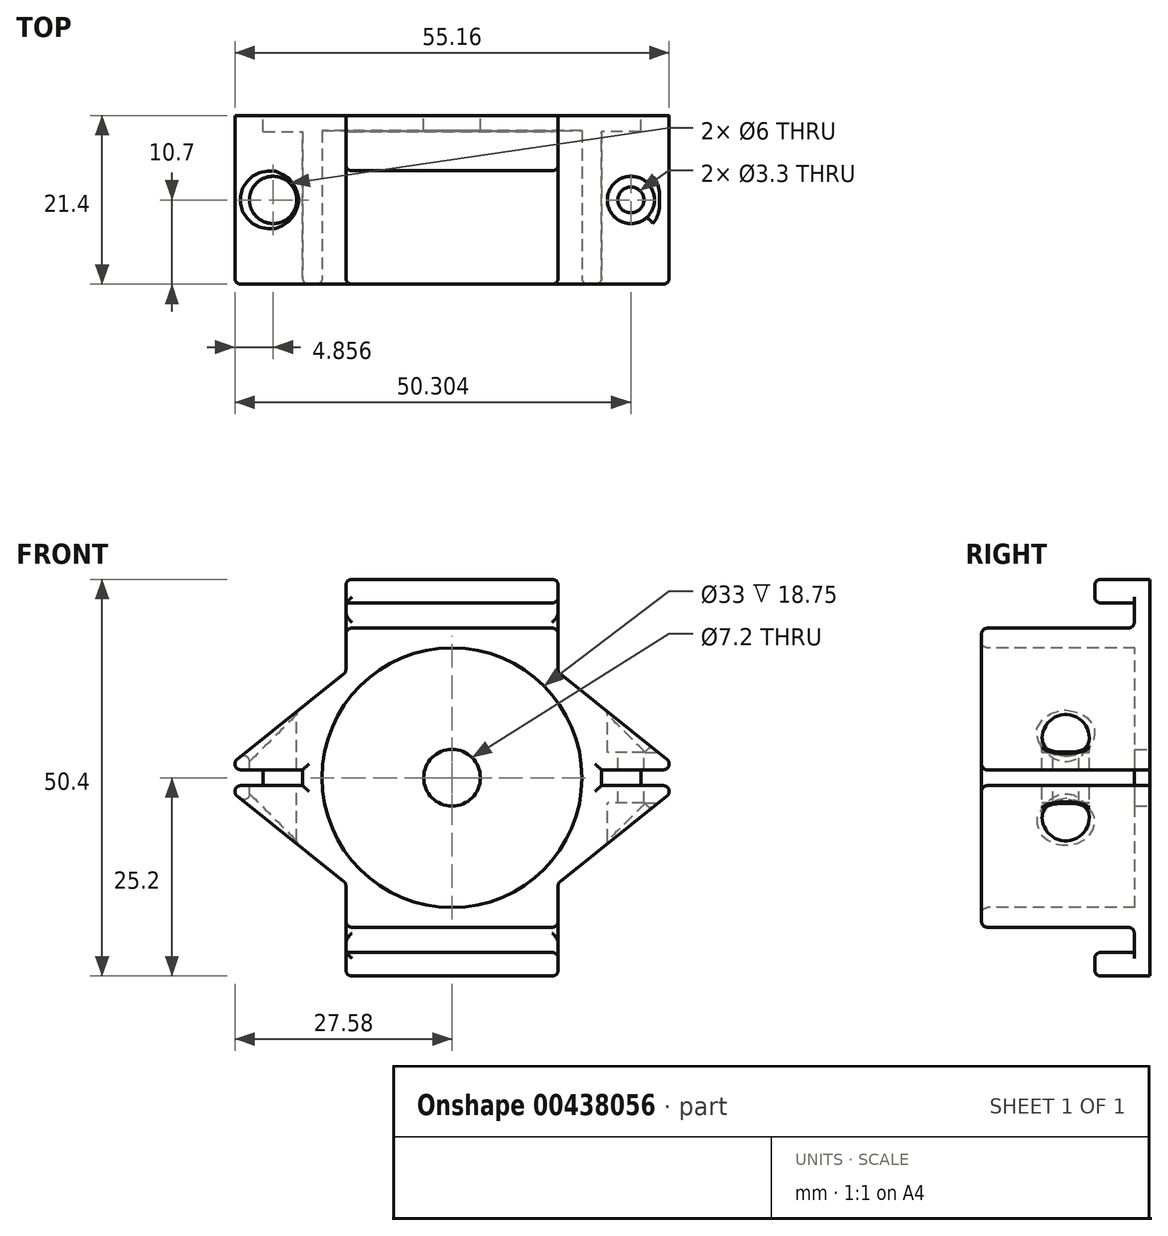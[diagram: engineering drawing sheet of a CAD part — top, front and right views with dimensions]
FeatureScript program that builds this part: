
annotation { "Feature Type Name" : "Feature", "Feature Type Description" : "" }
export const myFeature = defineFeature(function(context is Context, id is Id, definition is map)
    precondition{}
    {
        {
            var Q0;
            Q0=qCreatedBy(makeId("Front.planeOp"),FACE);
            var sketch = newSketch(context, id + "F0", { "sketchPlane" : qUnion([Q0])});
            skCircle(sketch, "E0", {"center": v(0, 0) * mm, "radius": 19 * mm});
            skSolve(sketch);
        }
        {
            var Q0;
            Q0=makeQuery(id+"F0.imprint","IMPRINT",FACE,{"disambiguationData":[TD([[makeQuery(id+"F0.imprint","IMPRINT",EDGE,{"derivedFrom":sQuery(id+"F0.wireOp",EDGE,"E0")}),1.0]])]});
            extrude(context, id + "F1", {"entities" : qUnion([Q0]), "depth" : (19.5 + 1.9) * mm});
        }
        {
            var Q0;
            Q0=makeQuery(id+"F1.opExtrude","CAP_FACE",FACE,{"disambiguationData":[OSD([sQuery(id+"F0.wireOp",EDGE,"E0")])],"isStart":false});
            var sketch = newSketch(context, id + "F2", { "sketchPlane" : qUnion([Q0])});
            skCircle(sketch, "E1", {"center": v(0, 0) * mm, "radius": 16.5 * mm});
            skSolve(sketch);
        }
        {
            var Q0;
            Q0=makeQuery(id+"F2.imprint","IMPRINT",FACE,{"disambiguationData":[TD([[makeQuery(id+"F2.imprint","IMPRINT",EDGE,{"derivedFrom":sQuery(id+"F2.wireOp",EDGE,"E1")}),1.0]])]});
            var Q1;
            Q1=sQuery(id+"F2.wireOp",EDGE,"E1");
            extrude(context, id + "F3", {"entities" : qUnion([Q0]), "operationType" : NewBodyOperationType.REMOVE, "surfaceEntities" : qUnion([Q1]), "oppositeDirection" : true, "depth" : 19.5 * mm});
        }
        {
            var Q0;
            Q0=makeQuery(id+"F0.imprint","IMPRINT",FACE,{"disambiguationData":[TD([[makeQuery(id+"F0.imprint","IMPRINT",EDGE,{"derivedFrom":sQuery(id+"F0.wireOp",EDGE,"E0")}),1.0]])]});
            var sketch = newSketch(context, id + "F4", { "sketchPlane" : qUnion([Q0])});
            skCircle(sketch, "E2", {"center": v(0, 0) * mm, "radius": 3.6 * mm});
            skSolve(sketch);
        }
        {
            var Q0;
            Q0=makeQuery(id+"F4.imprint","IMPRINT",FACE,{"disambiguationData":[TD([[makeQuery(id+"F4.imprint","IMPRINT",EDGE,{"derivedFrom":sQuery(id+"F4.wireOp",EDGE,"E2")}),1.0]])]});
            extrude(context, id + "F5", {"entities" : qUnion([Q0]), "operationType" : NewBodyOperationType.REMOVE, "oppositeDirection" : true, "depth" : -1.9 * mm});
        }
        {
            var Q0;
            {var subQ0=sQuery(id+"F0.wireOp",EDGE,"E0");Q0=makeQuery(id+"F8.boolean.opBoolean","MERGE",FACE,{"derivedFrom":[makeQuery(id+"F1.opExtrude","CAP_FACE",FACE,{"disambiguationData":[OSD([subQ0])],"isStart":false}),makeQuery(id+"F8.opExtrude","CAP_FACE",FACE,{"disambiguationData":[OSD([subQ0,sQuery(id+"F7.wireOp",EDGE,"JnGJQQhQ-O3qH-GfFH-OKy3-jtoUdUrH5ozl"),sQuery(id+"F7.wireOp",EDGE,"E11")])],"isStart":true}),makeQuery(id+"F8.opExtrude","CAP_FACE",FACE,{"disambiguationData":[OSD([subQ0,sQuery(id+"F7.wireOp",EDGE,"b05943de-8eb0-47d5-9eb4-3e9c2a586c67.1.1"),sQuery(id+"F7.wireOp",EDGE,"b05943de-8eb0-47d5-9eb4-3e9c2a586c67.1.2")])],"isStart":true}),makeQuery(id+"F8.opExtrude","CAP_FACE",FACE,{"disambiguationData":[OSD([subQ0,sQuery(id+"F7.wireOp",EDGE,"76fbe852-51aa-46ac-98ce-1b56ffee6fad0.MirrorCS"),sQuery(id+"F7.wireOp",EDGE,"c90fd7eb-af4d-439f-be0f-882f93c487a10.MirrorCS")])],"isStart":true}),makeQuery(id+"F8.opExtrude","CAP_FACE",FACE,{"disambiguationData":[OSD([subQ0,sQuery(id+"F7.wireOp",EDGE,"384a4ab6-6deb-44a3-bccf-448af2679dce0.MirrorCS"),sQuery(id+"F7.wireOp",EDGE,"9e9dcbe8-0e53-4627-bc9e-6be6067dd5380.MirrorCS")])],"isStart":true})]});}
            var sketch = newSketch(context, id + "F6", { "sketchPlane" : qUnion([Q0])});
            skPoint(sketch, "E3.oppositeSnap0", {"position": v(0, 19) * mm});
            skLineSegment(sketch, "E3.top", {"start": v(-13.48, 19) * mm, "end": v(13.48, 19) * mm});
            skLineSegment(sketch, "E3.left", {"start": v(-13.48, 13.39) * mm, "end": v(-13.48, 19) * mm});
            skLineSegment(sketch, "E3.right", {"start": v(13.48, 13.39) * mm, "end": v(13.48, 19) * mm});
            skLineSegment(sketch, "E4", {"start": v(0, 19) * mm, "end": v(13.48, 13.39) * mm});
            skLineSegment(sketch, "E5", {"start": v(0, 19) * mm, "end": v(-13.48, 13.39) * mm});
            skLineSegment(sketch, "E6.MirrorCS", {"start": v(-13.48, -19) * mm, "end": v(13.48, -19) * mm});
            skLineSegment(sketch, "E7.MirrorCS", {"start": v(13.48, -13.39) * mm, "end": v(13.48, -19) * mm});
            skLineSegment(sketch, "E8.MirrorCS", {"start": v(0, -19) * mm, "end": v(13.48, -13.39) * mm});
            skLineSegment(sketch, "E9.MirrorCS", {"start": v(0, -19) * mm, "end": v(-13.48, -13.39) * mm});
            skLineSegment(sketch, "E10.MirrorCS", {"start": v(-13.48, -13.39) * mm, "end": v(-13.48, -19) * mm});
            skSolve(sketch);
        }
        {
            var Q0;
            Q0=makeQuery(id+"F1.opExtrude","CAP_FACE",FACE,{"disambiguationData":[OSD([sQuery(id+"F0.wireOp",EDGE,"E0")])],"isStart":false});
            var sketch = newSketch(context, id + "F7", { "sketchPlane" : qUnion([Q0])});
            skLineSegment(sketch, "E11", {"start": v(28.97, 1) * mm, "end": v(18.97, 1) * mm});
            skLineSegment(sketch, "E12", {"start": v(18.97, 1) * mm, "end": v(13.48, 13.39) * mm});
            skLineSegment(sketch, "E13", {"start": v(13.48, 13.39) * mm, "end": v(28.97, 1) * mm});
            skLineSegment(sketch, "E14.MirrorCS", {"start": v(-18.97, 1) * mm, "end": v(-13.48, 13.39) * mm});
            skLineSegment(sketch, "E15.MirrorCS", {"start": v(-13.48, 13.39) * mm, "end": v(-28.97, 1) * mm});
            skLineSegment(sketch, "E16.MirrorCS", {"start": v(-28.97, 1) * mm, "end": v(-18.97, 1) * mm});
            skLineSegment(sketch, "E17.MirrorCS", {"start": v(28.97, -1) * mm, "end": v(18.97, -1) * mm});
            skLineSegment(sketch, "E18.MirrorCS", {"start": v(13.48, -13.39) * mm, "end": v(28.97, -1) * mm});
            skLineSegment(sketch, "E19.MirrorCS", {"start": v(18.97, -1) * mm, "end": v(13.48, -13.39) * mm});
            skLineSegment(sketch, "E20.MirrorCS", {"start": v(-18.97, -1) * mm, "end": v(-13.48, -13.39) * mm});
            skLineSegment(sketch, "E21.MirrorCS", {"start": v(-13.48, -13.39) * mm, "end": v(-28.97, -1) * mm});
            skLineSegment(sketch, "E22.MirrorCS", {"start": v(-28.97, -1) * mm, "end": v(-18.97, -1) * mm});
            skSolve(sketch);
        }
        {
            var Q0;
            {var subQ0=sQuery(id+"F7.wireOp",EDGE,"JnGJQQhQ-O3qH-GfFH-OKy3-jtoUdUrH5ozl");Q0=makeQuery(id+"F7.imprint","IMPRINT",FACE,{"disambiguationData":[TD([[makeQuery(id+"F7.imprint","IMPRINT",EDGE,{"derivedFrom":subQ0}),-1.0]])]});}
            var Q1;
            {var subQ0=sQuery(id+"F7.wireOp",EDGE,"b05943de-8eb0-47d5-9eb4-3e9c2a586c67.1.1");Q1=makeQuery(id+"F7.imprint","IMPRINT",FACE,{"disambiguationData":[TD([[makeQuery(id+"F7.imprint","IMPRINT",EDGE,{"derivedFrom":subQ0}),-1.0]])]});}
            var Q2;
            {var subQ0=sQuery(id+"F7.wireOp",EDGE,"76fbe852-51aa-46ac-98ce-1b56ffee6fad0.MirrorCS");Q2=makeQuery(id+"F7.imprint","IMPRINT",FACE,{"disambiguationData":[TD([[makeQuery(id+"F7.imprint","IMPRINT",EDGE,{"derivedFrom":subQ0}),1.0]])]});}
            var Q3;
            {var subQ0=sQuery(id+"F7.wireOp",EDGE,"384a4ab6-6deb-44a3-bccf-448af2679dce0.MirrorCS");Q3=makeQuery(id+"F7.imprint","IMPRINT",FACE,{"disambiguationData":[TD([[makeQuery(id+"F7.imprint","IMPRINT",EDGE,{"derivedFrom":subQ0}),1.0]])]});}
            var Q4;
            {var subQ0=sQuery(id+"F6.wireOp",EDGE,"E3.left");Q4=makeQuery(id+"F6.imprint","IMPRINT",FACE,{"disambiguationData":[TD([[makeQuery(id+"F6.imprint","IMPRINT",EDGE,{"derivedFrom":subQ0}),-1.0]])]});}
            var Q5;
            {var subQ0=sQuery(id+"F6.wireOp",EDGE,"E3.right");Q5=makeQuery(id+"F6.imprint","IMPRINT",FACE,{"disambiguationData":[TD([[makeQuery(id+"F6.imprint","IMPRINT",EDGE,{"derivedFrom":subQ0}),1.0]])]});}
            var Q6;
            {var subQ0=sQuery(id+"F6.wireOp",EDGE,"E10.MirrorCS");Q6=makeQuery(id+"F6.imprint","IMPRINT",FACE,{"disambiguationData":[TD([[makeQuery(id+"F6.imprint","IMPRINT",EDGE,{"derivedFrom":subQ0}),1.0]])]});}
            var Q7;
            {var subQ0=sQuery(id+"F6.wireOp",EDGE,"E7.MirrorCS");Q7=makeQuery(id+"F6.imprint","IMPRINT",FACE,{"disambiguationData":[TD([[makeQuery(id+"F6.imprint","IMPRINT",EDGE,{"derivedFrom":subQ0}),-1.0]])]});}
            var Q8;
            {var subQ0=sQuery(id+"F7.wireOp",EDGE,"E15.MirrorCS");Q8=makeQuery(id+"F7.imprint","IMPRINT",FACE,{"disambiguationData":[TD([[makeQuery(id+"F7.imprint","IMPRINT",EDGE,{"derivedFrom":subQ0}),1.0]])]});}
            var Q9;
            {var subQ0=sQuery(id+"F7.wireOp",EDGE,"E21.MirrorCS");Q9=makeQuery(id+"F7.imprint","IMPRINT",FACE,{"disambiguationData":[TD([[makeQuery(id+"F7.imprint","IMPRINT",EDGE,{"derivedFrom":subQ0}),-1.0]])]});}
            var Q10;
            {var subQ0=sQuery(id+"F7.wireOp",EDGE,"E17.MirrorCS");Q10=makeQuery(id+"F7.imprint","IMPRINT",FACE,{"disambiguationData":[TD([[makeQuery(id+"F7.imprint","IMPRINT",EDGE,{"derivedFrom":subQ0}),1.0]])]});}
            var Q11;
            {var subQ0=sQuery(id+"F7.wireOp",EDGE,"E11");Q11=makeQuery(id+"F7.imprint","IMPRINT",FACE,{"disambiguationData":[TD([[makeQuery(id+"F7.imprint","IMPRINT",EDGE,{"derivedFrom":subQ0}),-1.0]])]});}
            var Q12;
            Q12=makeQuery(id+"F1.opExtrude","SWEPT_FACE",FACE,{"disambiguationData":[OSD([sQuery(id+"F0.wireOp",EDGE,"E0")])]});
            extrude(context, id + "F8", {"entities" : qUnion([Q0, Q1, Q2, Q3, Q4, Q5, Q6, Q7, Q8, Q9, Q10, Q11]), "operationType" : NewBodyOperationType.ADD, "oppositeDirection" : true, "endBoundEntityFace" : qUnion([Q12]), "depth" : (19.5 + 1.9) * mm});
        }
        {
            var Q0;
            Q0=qCreatedBy(makeId("Top.planeOp"),FACE);
            var sketch = newSketch(context, id + "F9", { "sketchPlane" : qUnion([Q0])});
            skCircle(sketch, "E23", {"center": v(22.72, -10.7) * mm, "radius": 3 * mm});
            skCircle(sketch, "E24.MirrorC", {"center": v(-22.72, -10.7) * mm, "radius": 3 * mm});
            skSolve(sketch);
        }
        {
            var Q0;
            Q0 = qSketchRegion(id + "F9", true);
            extrude(context, id + "F10", {"entities" : qUnion([Q0]), "operationType" : NewBodyOperationType.REMOVE, "oppositeDirection" : true, "depth" : 20.52 * mm, "symmetric" : true});
        }
        {
            var Q0;
            Q0=makeQuery(id+"F9.imprint","IMPRINT",FACE,{"disambiguationData":[TD([[makeQuery(id+"F9.imprint","IMPRINT",EDGE,{"derivedFrom":sQuery(id+"F9.wireOp",EDGE,"E23")}),1.0]])]});
            var Q1;
            Q1=makeQuery(id+"F9.imprint","IMPRINT",FACE,{"disambiguationData":[TD([[makeQuery(id+"F9.imprint","IMPRINT",EDGE,{"derivedFrom":sQuery(id+"F9.wireOp",EDGE,"E24.MirrorC")}),-1.0]])]});
            extrude(context, id + "F11", {"entities" : qUnion([Q0, Q1]), "operationType" : NewBodyOperationType.ADD, "oppositeDirection" : true, "depth" : 6.44 * mm, "symmetric" : true});
        }
        {
            var Q0;
            Q0 = qSketchRegion(id + "F9", true);
            extrude(context, id + "F12", {"entities" : qUnion([Q0]), "operationType" : NewBodyOperationType.REMOVE, "depth" : 2 * mm, "symmetric" : true});
        }
        {
            var Q0;
            Q0=qCreatedBy(makeId("Top.planeOp"),FACE);
            var sketch = newSketch(context, id + "F13", { "sketchPlane" : qUnion([Q0])});
            skCircle(sketch, "E25", {"center": v(22.72, -10.7) * mm, "radius": 1.65 * mm});
            skCircle(sketch, "E26.MirrorC", {"center": v(-22.72, -10.7) * mm, "radius": 1.65 * mm});
            skSolve(sketch);
        }
        {
            var Q0;
            Q0=makeQuery(id+"F13.imprint","IMPRINT",FACE,{"disambiguationData":[TD([[makeQuery(id+"F13.imprint","IMPRINT",EDGE,{"derivedFrom":sQuery(id+"F13.wireOp",EDGE,"E25")}),1.0]])]});
            var Q1;
            Q1=makeQuery(id+"F13.imprint","IMPRINT",FACE,{"disambiguationData":[TD([[makeQuery(id+"F13.imprint","IMPRINT",EDGE,{"derivedFrom":sQuery(id+"F13.wireOp",EDGE,"E26.MirrorC")}),-1.0]])]});
            extrude(context, id + "F14", {"entities" : qUnion([Q0, Q1]), "operationType" : NewBodyOperationType.REMOVE, "oppositeDirection" : true, "depth" : 20 * mm, "symmetric" : true});
        }
        {
            var Q0;
            {var subQ0=sQuery(id+"F6.wireOp",EDGE,"E6.MirrorCS");var subQ1=sQuery(id+"F0.wireOp",EDGE,"E0");var subQ2=sQuery(id+"F6.wireOp",EDGE,"E3.top");Q0=makeQuery(id+"F8.boolean.opBoolean","MERGE",FACE,{"derivedFrom":[makeQuery(id+"F1.opExtrude","CAP_FACE",FACE,{"disambiguationData":[OSD([subQ1])],"isStart":true}),makeQuery(id+"F8.opExtrude","CAP_FACE",FACE,{"disambiguationData":[OSD([subQ1,sQuery(id+"F7.wireOp",EDGE,"JnGJQQhQ-O3qH-GfFH-OKy3-jtoUdUrH5ozl"),sQuery(id+"F7.wireOp",EDGE,"E11")])],"isStart":false}),makeQuery(id+"F8.opExtrude","CAP_FACE",FACE,{"disambiguationData":[OSD([subQ1,sQuery(id+"F7.wireOp",EDGE,"b05943de-8eb0-47d5-9eb4-3e9c2a586c67.1.1"),sQuery(id+"F7.wireOp",EDGE,"b05943de-8eb0-47d5-9eb4-3e9c2a586c67.1.2")])],"isStart":false}),makeQuery(id+"F8.opExtrude","CAP_FACE",FACE,{"disambiguationData":[OSD([subQ1,sQuery(id+"F7.wireOp",EDGE,"76fbe852-51aa-46ac-98ce-1b56ffee6fad0.MirrorCS"),sQuery(id+"F7.wireOp",EDGE,"c90fd7eb-af4d-439f-be0f-882f93c487a10.MirrorCS")])],"isStart":false}),makeQuery(id+"F8.opExtrude","CAP_FACE",FACE,{"disambiguationData":[OSD([subQ1,sQuery(id+"F7.wireOp",EDGE,"384a4ab6-6deb-44a3-bccf-448af2679dce0.MirrorCS"),sQuery(id+"F7.wireOp",EDGE,"9e9dcbe8-0e53-4627-bc9e-6be6067dd5380.MirrorCS")])],"isStart":false}),makeQuery(id+"F8.opExtrude","CAP_FACE",FACE,{"disambiguationData":[OSD([subQ1,subQ2,sQuery(id+"F6.wireOp",EDGE,"E3.left")])],"isStart":false}),makeQuery(id+"F8.opExtrude","CAP_FACE",FACE,{"disambiguationData":[OSD([subQ1,subQ2,sQuery(id+"F6.wireOp",EDGE,"E3.right")])],"isStart":false}),makeQuery(id+"F8.opExtrude","CAP_FACE",FACE,{"disambiguationData":[OSD([subQ1,subQ0,sQuery(id+"F6.wireOp",EDGE,"E10.MirrorCS")])],"isStart":false}),makeQuery(id+"F8.opExtrude","CAP_FACE",FACE,{"disambiguationData":[OSD([subQ1,subQ0,sQuery(id+"F6.wireOp",EDGE,"E7.MirrorCS")])],"isStart":false})]});}
            var sketch = newSketch(context, id + "F15", { "sketchPlane" : qUnion([Q0])});
            skLineSegment(sketch, "E27.bottom", {"start": v(-13.48, 19) * mm, "end": v(13.48, 19) * mm});
            skLineSegment(sketch, "E27.top", {"start": v(-13.48, 22.2) * mm, "end": v(13.48, 22.2) * mm});
            skLineSegment(sketch, "E27.left", {"start": v(-13.48, 19) * mm, "end": v(-13.48, 22.2) * mm});
            skLineSegment(sketch, "E27.right", {"start": v(13.48, 19) * mm, "end": v(13.48, 22.2) * mm});
            skLineSegment(sketch, "E28.MirrorCS", {"start": v(-13.48, -19) * mm, "end": v(-13.48, -22.2) * mm});
            skLineSegment(sketch, "E29.MirrorCS", {"start": v(-13.48, -22.2) * mm, "end": v(13.48, -22.2) * mm});
            skLineSegment(sketch, "E30.MirrorCS", {"start": v(-13.48, -19) * mm, "end": v(13.48, -19) * mm});
            skLineSegment(sketch, "E31.MirrorCS", {"start": v(13.48, -19) * mm, "end": v(13.48, -22.2) * mm});
            skLineSegment(sketch, "E32.bottom", {"start": v(-18.97, 1) * mm, "end": v(-23.97, 1) * mm});
            skLineSegment(sketch, "E32.top", {"start": v(-18.97, -1) * mm, "end": v(-23.97, -1) * mm});
            skLineSegment(sketch, "E32.left", {"start": v(-18.97, 1) * mm, "end": v(-18.97, -1) * mm});
            skLineSegment(sketch, "E32.right", {"start": v(-23.97, 1) * mm, "end": v(-23.97, -1) * mm});
            skPoint(sketch, "E33", {"position": v(-23.97, 1) * mm});
            skPoint(sketch, "E34", {"position": v(-23.97, -1) * mm});
            skLineSegment(sketch, "E35.bottom", {"start": v(18.97, 1) * mm, "end": v(23.97, 1) * mm});
            skLineSegment(sketch, "E35.top", {"start": v(18.97, -1) * mm, "end": v(23.97, -1) * mm});
            skLineSegment(sketch, "E35.left", {"start": v(18.97, 1) * mm, "end": v(18.97, -1) * mm});
            skLineSegment(sketch, "E35.right", {"start": v(23.97, 1) * mm, "end": v(23.97, -1) * mm});
            skPoint(sketch, "E36", {"position": v(23.97, 1) * mm});
            skPoint(sketch, "E37", {"position": v(23.97, -1) * mm});
            skSolve(sketch);
        }
        {
            var Q0;
            Q0=makeQuery(id+"F15.imprint","IMPRINT",FACE,{"disambiguationData":[TD([[makeQuery(id+"F15.imprint","IMPRINT",EDGE,{"derivedFrom":sQuery(id+"F15.wireOp",EDGE,"E27.bottom")}),-1.0]])]});
            var sketch = newSketch(context, id + "F16", { "sketchPlane" : qUnion([Q0])});
            skLineSegment(sketch, "E38.bottom", {"start": v(-13.48, 22.2) * mm, "end": v(13.48, 22.2) * mm});
            skLineSegment(sketch, "E38.top", {"start": v(-13.48, 25.2) * mm, "end": v(13.48, 25.2) * mm});
            skLineSegment(sketch, "E38.left", {"start": v(-13.48, 22.2) * mm, "end": v(-13.48, 25.2) * mm});
            skLineSegment(sketch, "E38.right", {"start": v(13.48, 22.2) * mm, "end": v(13.48, 25.2) * mm});
            skLineSegment(sketch, "E39.MirrorCS", {"start": v(-13.48, -22.2) * mm, "end": v(13.48, -22.2) * mm});
            skLineSegment(sketch, "E40.MirrorCS", {"start": v(13.48, -22.2) * mm, "end": v(13.48, -25.2) * mm});
            skLineSegment(sketch, "E41.MirrorCS", {"start": v(-13.48, -25.2) * mm, "end": v(13.48, -25.2) * mm});
            skLineSegment(sketch, "E42.MirrorCS", {"start": v(-13.48, -22.2) * mm, "end": v(-13.48, -25.2) * mm});
            skSolve(sketch);
        }
        {
            var Q0;
            Q0=makeQuery(id+"F15.imprint","IMPRINT",FACE,{"disambiguationData":[TD([[makeQuery(id+"F15.imprint","IMPRINT",EDGE,{"derivedFrom":sQuery(id+"F15.wireOp",EDGE,"E27.bottom")}),-1.0]])]});
            var Q1;
            Q1=makeQuery(id+"F15.imprint","IMPRINT",FACE,{"disambiguationData":[TD([[makeQuery(id+"F15.imprint","IMPRINT",EDGE,{"derivedFrom":sQuery(id+"F15.wireOp",EDGE,"pVymzZib-BWJs-xoJs-sTC6-ayV31QzRr0Km.bottom")}),1.0]])]});
            var Q2;
            Q2=makeQuery(id+"F15.imprint","IMPRINT",FACE,{"disambiguationData":[TD([[makeQuery(id+"F15.imprint","IMPRINT",EDGE,{"derivedFrom":sQuery(id+"F15.wireOp",EDGE,"E28.MirrorCS")}),1.0]])]});
            var Q3;
            Q3=makeQuery(id+"F15.imprint","IMPRINT",FACE,{"disambiguationData":[TD([[makeQuery(id+"F15.imprint","IMPRINT",EDGE,{"derivedFrom":sQuery(id+"F15.wireOp",EDGE,"p6bBq81N-0zO1-3e9F-RNQn-4i8wIQgML4Y9.bottom")}),-1.0]])]});
            var Q4;
            Q4=makeQuery(id+"F15.imprint","IMPRINT",FACE,{"disambiguationData":[TD([[makeQuery(id+"F15.imprint","IMPRINT",EDGE,{"derivedFrom":sQuery(id+"F15.wireOp",EDGE,"SPB9DOaG-sIQF-bfla-kVRV-wDr5gLPkeSE0.bottom")}),1.0]])]});
            var Q5;
            Q5=makeQuery(id+"F15.imprint","IMPRINT",FACE,{"disambiguationData":[TD([[makeQuery(id+"F15.imprint","IMPRINT",EDGE,{"derivedFrom":sQuery(id+"F15.wireOp",EDGE,"49c1c15a-7392-4b62-8206-24bcfd820ca90.MirrorCS")}),1.0]])]});
            var Q6;
            Q6=makeQuery(id+"F15.imprint","IMPRINT",FACE,{"disambiguationData":[TD([[makeQuery(id+"F15.imprint","IMPRINT",EDGE,{"derivedFrom":sQuery(id+"F15.wireOp",EDGE,"E35.bottom")}),1.0]])]});
            var Q7;
            Q7=makeQuery(id+"F15.imprint","IMPRINT",FACE,{"disambiguationData":[TD([[makeQuery(id+"F15.imprint","IMPRINT",EDGE,{"derivedFrom":sQuery(id+"F15.wireOp",EDGE,"E32.bottom")}),-1.0]])]});
            extrude(context, id + "F17", {"entities" : qUnion([Q0, Q1, Q2, Q3, Q4, Q5, Q6, Q7]), "operationType" : NewBodyOperationType.ADD, "oppositeDirection" : true, "depth" : 2 * mm});
        }
        {
            var Q0;
            Q0=makeQuery(id+"F16.imprint","IMPRINT",FACE,{"disambiguationData":[TD([[makeQuery(id+"F16.imprint","IMPRINT",EDGE,{"derivedFrom":sQuery(id+"F16.wireOp",EDGE,"E39.MirrorCS")}),-1.0]])]});
            var Q1;
            Q1=makeQuery(id+"F16.imprint","IMPRINT",FACE,{"disambiguationData":[TD([[makeQuery(id+"F16.imprint","IMPRINT",EDGE,{"derivedFrom":sQuery(id+"F16.wireOp",EDGE,"E38.bottom")}),1.0]])]});
            extrude(context, id + "F18", {"entities" : qUnion([Q0, Q1]), "operationType" : NewBodyOperationType.ADD, "oppositeDirection" : true, "depth" : 7 * mm});
        }
        {
            var Q0;
            {var subQ0=sQuery(id+"F0.wireOp",EDGE,"E0");var subQ1=sQuery(id+"F6.wireOp",EDGE,"E6.MirrorCS");var subQ2=sQuery(id+"F6.wireOp",EDGE,"E3.top");Q0=makeQuery(id+"F8.boolean.opBoolean","MERGE",FACE,{"derivedFrom":[makeQuery(id+"F1.opExtrude","CAP_FACE",FACE,{"disambiguationData":[OSD([subQ0])],"isStart":false}),makeQuery(id+"F8.opExtrude","CAP_FACE",FACE,{"disambiguationData":[OSD([subQ0,subQ2,sQuery(id+"F6.wireOp",EDGE,"E3.left")])],"isStart":true}),makeQuery(id+"F8.opExtrude","CAP_FACE",FACE,{"disambiguationData":[OSD([subQ0,subQ2,sQuery(id+"F6.wireOp",EDGE,"E3.right")])],"isStart":true}),makeQuery(id+"F8.opExtrude","CAP_FACE",FACE,{"disambiguationData":[OSD([subQ0,subQ1,sQuery(id+"F6.wireOp",EDGE,"E10.MirrorCS")])],"isStart":true}),makeQuery(id+"F8.opExtrude","CAP_FACE",FACE,{"disambiguationData":[OSD([subQ0,subQ1,sQuery(id+"F6.wireOp",EDGE,"E7.MirrorCS")])],"isStart":true}),makeQuery(id+"F8.opExtrude","CAP_FACE",FACE,{"disambiguationData":[OSD([subQ0,sQuery(id+"F7.wireOp",EDGE,"E11"),sQuery(id+"F7.wireOp",EDGE,"E13")])],"isStart":true}),makeQuery(id+"F8.opExtrude","CAP_FACE",FACE,{"disambiguationData":[OSD([subQ0,sQuery(id+"F7.wireOp",EDGE,"E15.MirrorCS"),sQuery(id+"F7.wireOp",EDGE,"E16.MirrorCS")])],"isStart":true}),makeQuery(id+"F8.opExtrude","CAP_FACE",FACE,{"disambiguationData":[OSD([subQ0,sQuery(id+"F7.wireOp",EDGE,"E17.MirrorCS"),sQuery(id+"F7.wireOp",EDGE,"E18.MirrorCS")])],"isStart":true}),makeQuery(id+"F8.opExtrude","CAP_FACE",FACE,{"disambiguationData":[OSD([subQ0,sQuery(id+"F7.wireOp",EDGE,"E21.MirrorCS"),sQuery(id+"F7.wireOp",EDGE,"E22.MirrorCS")])],"isStart":true})]});}
            var Q1;
            Q1=makeQuery(id+"F10.boolean.opBoolean","INTERSECT",EDGE,{"derivedFrom":[makeQuery(id+"F8.opExtrude","SWEPT_FACE",FACE,{"disambiguationData":[OSD([sQuery(id+"F7.wireOp",EDGE,"E18.MirrorCS")])]}),makeQuery(id+"F10.opExtrude","SWEPT_FACE",FACE,{"disambiguationData":[OSD([sQuery(id+"F9.wireOp",EDGE,"E23")])]})]});
            var Q2;
            Q2=makeQuery(id+"F10.boolean.opBoolean","INTERSECT",EDGE,{"derivedFrom":[makeQuery(id+"F8.opExtrude","SWEPT_FACE",FACE,{"disambiguationData":[OSD([sQuery(id+"F7.wireOp",EDGE,"E13")])]}),makeQuery(id+"F10.opExtrude","SWEPT_FACE",FACE,{"disambiguationData":[OSD([sQuery(id+"F9.wireOp",EDGE,"E23")])]})]});
            var Q3;
            Q3=makeQuery(id+"F18.opExtrude","CAP_FACE",FACE,{"disambiguationData":[OSD([sQuery(id+"F16.wireOp",EDGE,"E39.MirrorCS"),sQuery(id+"F16.wireOp",EDGE,"E40.MirrorCS"),sQuery(id+"F16.wireOp",EDGE,"E41.MirrorCS"),sQuery(id+"F16.wireOp",EDGE,"E42.MirrorCS")])],"isStart":false});
            var Q4;
            {var subQ0=sQuery(id+"F6.wireOp",EDGE,"E6.MirrorCS");Q4=makeQuery(id+"F8.boolean.opBoolean","MERGE",FACE,{"derivedFrom":[makeQuery(id+"F8.opExtrude","SWEPT_FACE",FACE,{"disambiguationData":[OSD([subQ0]),TDD([makeQuery(id+"F6.imprint","IMPRINT",EDGE,{"disambiguationData":[TD([[makeQuery(id+"F6.imprint","INTERSECT",VERTEX,{"derivedFrom":[subQ0,sQuery(id+"F6.wireOp",EDGE,"E10.MirrorCS")]}),-1.0]])],"derivedFrom":subQ0})])]}),makeQuery(id+"F8.opExtrude","SWEPT_FACE",FACE,{"disambiguationData":[OSD([subQ0]),TDD([makeQuery(id+"F6.imprint","IMPRINT",EDGE,{"disambiguationData":[TD([[makeQuery(id+"F6.imprint","INTERSECT",VERTEX,{"derivedFrom":[subQ0,sQuery(id+"F6.wireOp",EDGE,"E7.MirrorCS")]}),1.0]])],"derivedFrom":subQ0})])]})]});}
            var Q5;
            {var subQ0=sQuery(id+"F6.wireOp",EDGE,"E3.top");Q5=makeQuery(id+"F8.boolean.opBoolean","MERGE",FACE,{"derivedFrom":[makeQuery(id+"F8.opExtrude","SWEPT_FACE",FACE,{"disambiguationData":[OSD([subQ0]),TDD([makeQuery(id+"F6.imprint","IMPRINT",EDGE,{"disambiguationData":[TD([[makeQuery(id+"F6.imprint","INTERSECT",VERTEX,{"derivedFrom":[subQ0,sQuery(id+"F6.wireOp",EDGE,"E3.left")]}),-1.0]])],"derivedFrom":subQ0})])]}),makeQuery(id+"F8.opExtrude","SWEPT_FACE",FACE,{"disambiguationData":[OSD([subQ0]),TDD([makeQuery(id+"F6.imprint","IMPRINT",EDGE,{"disambiguationData":[TD([[makeQuery(id+"F6.imprint","INTERSECT",VERTEX,{"derivedFrom":[subQ0,sQuery(id+"F6.wireOp",EDGE,"E3.right")]}),1.0]])],"derivedFrom":subQ0})])]})]});}
            var Q6;
            Q6=makeQuery(id+"F18.opExtrude","CAP_FACE",FACE,{"disambiguationData":[OSD([sQuery(id+"F16.wireOp",EDGE,"E38.bottom"),sQuery(id+"F16.wireOp",EDGE,"E38.top"),sQuery(id+"F16.wireOp",EDGE,"E38.left"),sQuery(id+"F16.wireOp",EDGE,"E38.right")])],"isStart":false});
            var Q7;
            Q7=makeQuery(id+"F10.boolean.opBoolean","INTERSECT",EDGE,{"derivedFrom":[makeQuery(id+"F8.opExtrude","SWEPT_FACE",FACE,{"disambiguationData":[OSD([sQuery(id+"F7.wireOp",EDGE,"E15.MirrorCS")])]}),makeQuery(id+"F10.opExtrude","SWEPT_FACE",FACE,{"disambiguationData":[OSD([sQuery(id+"F9.wireOp",EDGE,"E24.MirrorC")])]})]});
            var Q8;
            Q8=makeQuery(id+"F10.boolean.opBoolean","INTERSECT",EDGE,{"derivedFrom":[makeQuery(id+"F8.opExtrude","SWEPT_FACE",FACE,{"disambiguationData":[OSD([sQuery(id+"F7.wireOp",EDGE,"E21.MirrorCS")])]}),makeQuery(id+"F10.opExtrude","SWEPT_FACE",FACE,{"disambiguationData":[OSD([sQuery(id+"F9.wireOp",EDGE,"E24.MirrorC")])]})]});
            var Q9;
            Q9=makeQuery(id+"F8.opExtrude","SWEPT_EDGE",EDGE,{"disambiguationData":[OSD([sQuery(id+"F7.wireOp",EDGE,"E21.MirrorCS"),sQuery(id+"F7.wireOp",EDGE,"E22.MirrorCS")])]});
            var Q10;
            Q10=makeQuery(id+"F8.opExtrude","SWEPT_EDGE",EDGE,{"disambiguationData":[OSD([sQuery(id+"F7.wireOp",EDGE,"E15.MirrorCS"),sQuery(id+"F7.wireOp",EDGE,"E16.MirrorCS")])]});
            var Q11;
            Q11=makeQuery(id+"F8.opExtrude","SWEPT_EDGE",EDGE,{"disambiguationData":[OSD([sQuery(id+"F7.wireOp",EDGE,"E11"),sQuery(id+"F7.wireOp",EDGE,"E13")])]});
            var Q12;
            Q12=makeQuery(id+"F8.opExtrude","SWEPT_EDGE",EDGE,{"disambiguationData":[OSD([sQuery(id+"F7.wireOp",EDGE,"E17.MirrorCS"),sQuery(id+"F7.wireOp",EDGE,"E18.MirrorCS")])]});
            var Q13;
            Q13=makeQuery(id+"F17.opExtrude","SWEPT_EDGE",EDGE,{"disambiguationData":[OSD([sQuery(id+"F7.wireOp",EDGE,"E17.MirrorCS"),sQuery(id+"F15.wireOp",EDGE,"E32.top"),sQuery(id+"F15.wireOp",EDGE,"E32.right")])]});
            var Q14;
            Q14=makeQuery(id+"F17.opExtrude","SWEPT_EDGE",EDGE,{"disambiguationData":[OSD([sQuery(id+"F7.wireOp",EDGE,"E11"),sQuery(id+"F15.wireOp",EDGE,"E32.bottom"),sQuery(id+"F15.wireOp",EDGE,"E32.right")])]});
            var Q15;
            Q15=makeQuery(id+"F18.opExtrude","SWEPT_EDGE",EDGE,{"disambiguationData":[OSD([sQuery(id+"F16.wireOp",EDGE,"E39.MirrorCS"),sQuery(id+"F16.wireOp",EDGE,"E42.MirrorCS")])]});
            var Q16;
            Q16=makeQuery(id+"F18.opExtrude","SWEPT_EDGE",EDGE,{"disambiguationData":[OSD([sQuery(id+"F16.wireOp",EDGE,"E41.MirrorCS"),sQuery(id+"F16.wireOp",EDGE,"E42.MirrorCS")])]});
            var Q17;
            Q17=makeQuery(id+"F17.opExtrude","CAP_EDGE",EDGE,{"disambiguationData":[OSD([sQuery(id+"F15.wireOp",EDGE,"E29.MirrorCS")])],"isStart":false});
            var Q18;
            Q18=makeQuery(id+"F17.opExtrude","CAP_EDGE",EDGE,{"disambiguationData":[OSD([sQuery(id+"F15.wireOp",EDGE,"E27.top")])],"isStart":false});
            var Q19;
            Q19=makeQuery(id+"F18.opExtrude","SWEPT_EDGE",EDGE,{"disambiguationData":[OSD([sQuery(id+"F15.wireOp",EDGE,"E27.left"),sQuery(id+"F16.wireOp",EDGE,"E38.bottom"),sQuery(id+"F16.wireOp",EDGE,"E38.left")])]});
            var Q20;
            Q20=makeQuery(id+"F18.opExtrude","SWEPT_EDGE",EDGE,{"disambiguationData":[OSD([sQuery(id+"F16.wireOp",EDGE,"E38.top"),sQuery(id+"F16.wireOp",EDGE,"E38.left")])]});
            var Q21;
            Q21=makeQuery(id+"F18.opExtrude","SWEPT_EDGE",EDGE,{"disambiguationData":[OSD([sQuery(id+"F16.wireOp",EDGE,"E38.top"),sQuery(id+"F16.wireOp",EDGE,"E38.right")])]});
            var Q22;
            {var subQ0=sQuery(id+"F0.wireOp",EDGE,"E0");Q22=makeQuery(id+"F8.boolean.opBoolean","MERGE",EDGE,{"derivedFrom":[makeQuery(id+"F8.opExtrude","SWEPT_EDGE",EDGE,{"disambiguationData":[OSD([subQ0,sQuery(id+"F6.wireOp",EDGE,"E3.left"),sQuery(id+"F6.wireOp",EDGE,"E5")])]}),makeQuery(id+"F8.opExtrude","SWEPT_EDGE",EDGE,{"disambiguationData":[OSD([subQ0,sQuery(id+"F7.wireOp",EDGE,"E14.MirrorCS"),sQuery(id+"F7.wireOp",EDGE,"E15.MirrorCS")])]})]});}
            var Q23;
            {var subQ0=sQuery(id+"F0.wireOp",EDGE,"E0");Q23=makeQuery(id+"F8.boolean.opBoolean","MERGE",EDGE,{"derivedFrom":[makeQuery(id+"F8.opExtrude","SWEPT_EDGE",EDGE,{"disambiguationData":[OSD([subQ0,sQuery(id+"F6.wireOp",EDGE,"E9.MirrorCS"),sQuery(id+"F6.wireOp",EDGE,"E10.MirrorCS")])]}),makeQuery(id+"F8.opExtrude","SWEPT_EDGE",EDGE,{"disambiguationData":[OSD([subQ0,sQuery(id+"F7.wireOp",EDGE,"E20.MirrorCS"),sQuery(id+"F7.wireOp",EDGE,"E21.MirrorCS")])]})]});}
            var Q24;
            {var subQ0=sQuery(id+"F0.wireOp",EDGE,"E0");Q24=makeQuery(id+"F8.boolean.opBoolean","MERGE",EDGE,{"derivedFrom":[makeQuery(id+"F8.opExtrude","SWEPT_EDGE",EDGE,{"disambiguationData":[OSD([subQ0,sQuery(id+"F6.wireOp",EDGE,"E7.MirrorCS"),sQuery(id+"F6.wireOp",EDGE,"E8.MirrorCS")])]}),makeQuery(id+"F8.opExtrude","SWEPT_EDGE",EDGE,{"disambiguationData":[OSD([subQ0,sQuery(id+"F7.wireOp",EDGE,"E18.MirrorCS"),sQuery(id+"F7.wireOp",EDGE,"E19.MirrorCS")])]})]});}
            var Q25;
            {var subQ0=sQuery(id+"F0.wireOp",EDGE,"E0");Q25=makeQuery(id+"F8.boolean.opBoolean","MERGE",EDGE,{"derivedFrom":[makeQuery(id+"F8.opExtrude","SWEPT_EDGE",EDGE,{"disambiguationData":[OSD([subQ0,sQuery(id+"F6.wireOp",EDGE,"E3.right"),sQuery(id+"F6.wireOp",EDGE,"E4")])]}),makeQuery(id+"F8.opExtrude","SWEPT_EDGE",EDGE,{"disambiguationData":[OSD([subQ0,sQuery(id+"F7.wireOp",EDGE,"E12"),sQuery(id+"F7.wireOp",EDGE,"E13")])]})]});}
            var Q26;
            Q26=makeQuery(id+"F17.opExtrude","SWEPT_EDGE",EDGE,{"disambiguationData":[OSD([sQuery(id+"F7.wireOp",EDGE,"E16.MirrorCS"),sQuery(id+"F15.wireOp",EDGE,"E35.bottom"),sQuery(id+"F15.wireOp",EDGE,"E35.right")])]});
            var Q27;
            Q27=makeQuery(id+"F18.opExtrude","SWEPT_EDGE",EDGE,{"disambiguationData":[OSD([sQuery(id+"F16.wireOp",EDGE,"E40.MirrorCS"),sQuery(id+"F16.wireOp",EDGE,"E41.MirrorCS")])]});
            var Q28;
            Q28=makeQuery(id+"F17.opExtrude","SWEPT_EDGE",EDGE,{"disambiguationData":[OSD([sQuery(id+"F7.wireOp",EDGE,"E22.MirrorCS"),sQuery(id+"F15.wireOp",EDGE,"E35.top"),sQuery(id+"F15.wireOp",EDGE,"E35.right")])]});
            fillet(context, id + "F19", {"entities" : qUnion([Q0, Q1, Q2, Q3, Q4, Q5, Q6, Q7, Q8, Q9, Q10, Q11, Q12, Q13, Q14, Q15, Q16, Q17, Q18, Q19, Q20, Q21, Q22, Q23, Q24, Q25, Q26, Q27, Q28]), "radius" : 0.75 * mm, "tangentPropagation" : true, "allowEdgeOverflow" : false});
        }
    });
